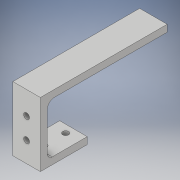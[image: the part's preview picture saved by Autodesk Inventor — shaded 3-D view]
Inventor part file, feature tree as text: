
AUTODESK INVENTOR PART (.ipt)
format: ipt  version: 2019 (Build 230136000, 136)  size: 141,824 bytes
history: native  units: in
note: dims shown in document units (in); Inventor stores cm internally (conversion verified against a paired STEP export)
features: extrude x3, sketch x3, fillet x2
ambient origin geometry x8: Origin, YZ Plane, XZ Plane, XY Plane, X Axis, Y Axis, Z Axis, Center Point
bodies: Solid1 (feature_tree)
feature tree (8):
  extrude  "Extrusion1"  Depth=0.85in
  extrude  "Extrusion2"  Depth=0.125in
  extrude  "Extrusion3"  Depth=0.125in
  fillet  "Fillet1"  Radius=2.3in
  fillet  "Fillet2"  Radius=0.107in
  sketch  "Sketch1"  dims[d0=0.125in d1=0.85in]
  sketch  "Sketch2"  dims[d2=0.5in d3=0.0in d4=0.125in]
  sketch  "Sketch3"  dims[d5=1.165in d6=0.125in d7=2.3in d8=0.107in d9=0.107in d10=0.25in d11=0.25in d12=0.379in d13=1.0in d14=0.0in d15=0.107in d16=0.107in d17=0.25in d18=0.25in d19=1.0in d20=0.0in d21=0.125in d22=0.09in d23=0.394in]
